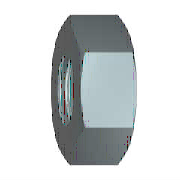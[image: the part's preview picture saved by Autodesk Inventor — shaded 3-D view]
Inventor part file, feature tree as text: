
AUTODESK INVENTOR PART (.ipt)
format: ipt  version: 2020 (Build 240168000, 168)  size: 165,376 bytes
history: native  units: mm (DEFAULTED — no unit token found)
features: sketch x3, other x2, extrude x1, hole x1, plane x1
ambient origin geometry x7: Origin, YZ Plane, XZ Plane, X Axis, Y Axis, Z Axis, Center Point
bodies: Solid1 (feature_tree)
feature tree (8):
  extrude  "Bryła"  Depth=9.237604mm
  other  "Faza1"
  hole  "Gwint"  [1 undecoded]
  other  "Work Axis1"
  plane  "Work Plane1"
  sketch  "Szkic1"
  sketch  "Szkic2"
  sketch  "Szkic3"
note: 1 required parameter value undecoded (feature->parameter linkage not recoverable at this tier; creation-order binding heuristic only, values carry confidence <= 0.55)
